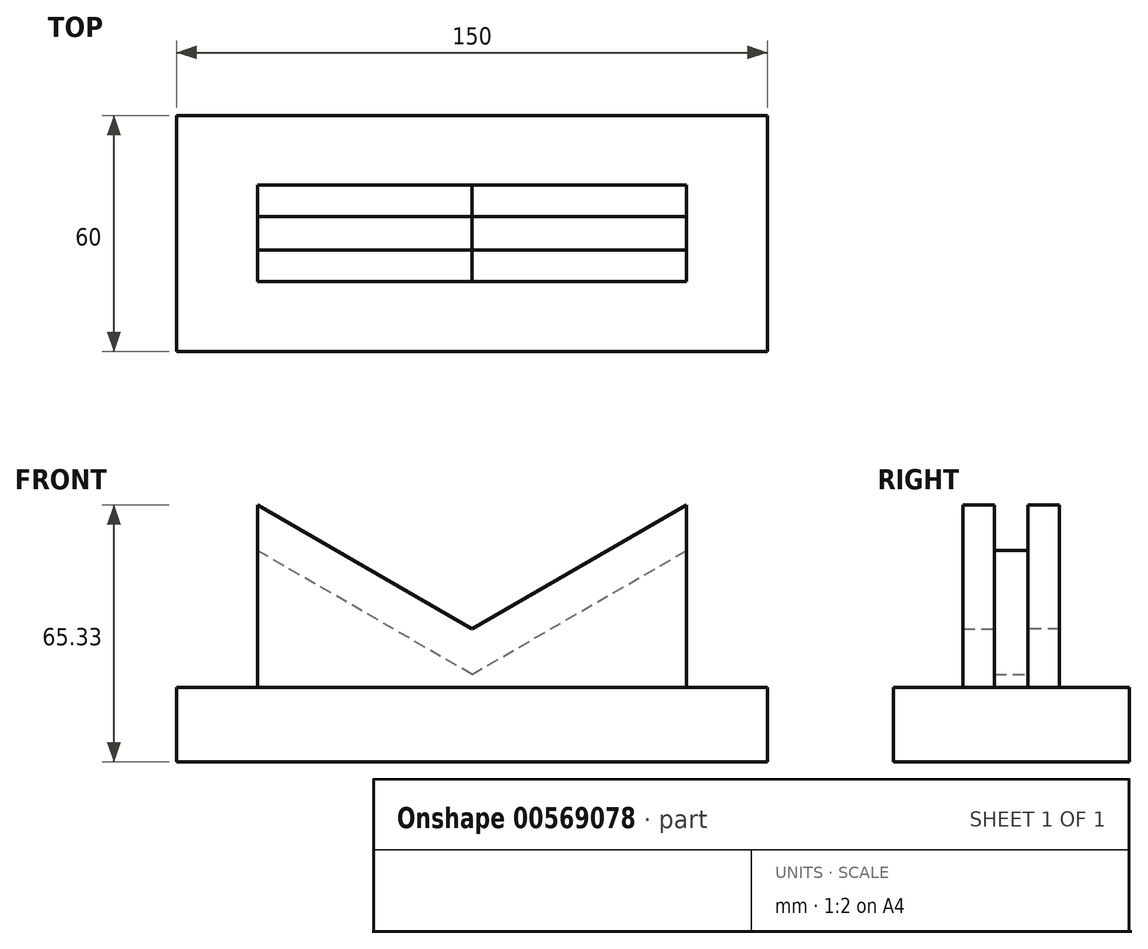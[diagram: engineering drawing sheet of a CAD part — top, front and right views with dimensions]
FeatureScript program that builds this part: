
annotation { "Feature Type Name" : "Feature", "Feature Type Description" : "" }
export const myFeature = defineFeature(function(context is Context, id is Id, definition is map)
    precondition{}
    {
        {
            var Q0;
            Q0=qCreatedBy(makeId("Front.planeOp"),FACE);
            var sketch = newSketch(context, id + "F0", { "sketchPlane" : qUnion([Q0])});
            skLineSegment(sketch, "E0.bottom", {"start": v(-75, 0) * mm, "end": v(75, 0) * mm});
            skLineSegment(sketch, "E0.top", {"start": v(-75, 19) * mm, "end": v(75, 19) * mm});
            skLineSegment(sketch, "E0.left", {"start": v(-75, 0) * mm, "end": v(-75, 19) * mm});
            skLineSegment(sketch, "E0.right", {"start": v(75, 0) * mm, "end": v(75, 19) * mm});
            skSolve(sketch);
        }
        {
            var Q0;
            Q0 = qSketchRegion(id + "F0", true);
            extrude(context, id + "F1", {"entities" : qUnion([Q0]), "endBound" : BoundingType.SYMMETRIC, "depth" : 60 * mm, "offsetDistance" : 25 * mm});
        }
        {
            var Q0;
            Q0=qCreatedBy(makeId("Front.planeOp"),FACE);
            var sketch = newSketch(context, id + "F2", { "sketchPlane" : qUnion([Q0])});
            skLineSegment(sketch, "E1", {"start": v(0, 22.3) * mm, "end": v(-54.53, 53.78) * mm});
            skLineSegment(sketch, "E2", {"start": v(-54.53, 53.78) * mm, "end": v(-54.53, 19) * mm});
            skLineSegment(sketch, "E3", {"start": v(0, 22.3) * mm, "end": v(0, 78.1) * mm, "construction": true});
            skLineSegment(sketch, "E4.MirrorCS", {"start": v(0, 22.3) * mm, "end": v(54.53, 53.78) * mm});
            skLineSegment(sketch, "E5.MirrorCS", {"start": v(54.53, 53.78) * mm, "end": v(54.53, 19) * mm});
            skPoint(sketch, "E6.orphan", {"position": v(54.53, 22.3) * mm});
            skPoint(sketch, "E7.orphan", {"position": v(-54.53, 22.3) * mm});
            skPoint(sketch, "E8.orphan", {"position": v(75, 19) * mm});
            skPoint(sketch, "E9.orphan", {"position": v(-75, 19) * mm});
            skLineSegment(sketch, "E10.0", {"start": v(-54.53, 19) * mm, "end": v(54.53, 19) * mm});
            skSolve(sketch);
        }
        {
            var Q0;
            Q0 = qSketchRegion(id + "F2", true);
            extrude(context, id + "F3", {"entities" : qUnion([Q0]), "endBound" : BoundingType.SYMMETRIC, "depth" : 8.5 * mm, "offsetDistance" : 25 * mm});
        }
        {
            var Q0;
            Q0=makeQuery(id+"F3.opExtrude","CAP_FACE",FACE,{"disambiguationData":[OSD([sQuery(id+"F2.wireOp",EDGE,"E1"),sQuery(id+"F2.wireOp",EDGE,"E2"),sQuery(id+"F2.wireOp",EDGE,"lnKhhqay-CDqk-tFTO-5ORt-z1OlfFbkKawb")])],"isStart":false});
            var sketch = newSketch(context, id + "F4", { "sketchPlane" : qUnion([Q0])});
            skLineSegment(sketch, "E11.0", {"start": v(0, 33.84) * mm, "end": v(-54.53, 65.33) * mm});
            skLineSegment(sketch, "E11.1", {"start": v(0, 33.84) * mm, "end": v(54.53, 65.33) * mm});
            skLineSegment(sketch, "E12.0", {"start": v(-54.53, 65.33) * mm, "end": v(-54.53, 19) * mm});
            skLineSegment(sketch, "E12.1", {"start": v(54.53, 65.33) * mm, "end": v(54.53, 19) * mm});
            skPoint(sketch, "E13.orphan", {"position": v(-54.53, 53.78) * mm});
            skPoint(sketch, "E14.orphan", {"position": v(54.53, 53.78) * mm});
            skLineSegment(sketch, "E15.0", {"start": v(-54.53, 19) * mm, "end": v(54.53, 19) * mm});
            skPoint(sketch, "E16.orphan", {"position": v(75, 19) * mm});
            skPoint(sketch, "E17.orphan", {"position": v(-75, 19) * mm});
            skSolve(sketch);
        }
        {
            var Q0;
            Q0 = qSketchRegion(id + "F4", true);
            extrude(context, id + "F5", {"entities" : qUnion([Q0]), "depth" : 8 * mm, "offsetDistance" : 25 * mm});
        }
        {
            var Q0;
            Q0=makeQuery(id+"F3.opExtrude","CAP_FACE",FACE,{"disambiguationData":[OSD([sQuery(id+"F2.wireOp",EDGE,"E4.MirrorCS"),sQuery(id+"F2.wireOp",EDGE,"E5.MirrorCS"),sQuery(id+"F2.wireOp",EDGE,"0fbee516-dda7-44bb-97da-947db9ab2e902.MirrorCS")])],"isStart":true});
            var sketch = newSketch(context, id + "F6", { "sketchPlane" : qUnion([Q0])});
            skLineSegment(sketch, "E18.0", {"start": v(54.53, 65.33) * mm, "end": v(54.53, 19) * mm});
            skLineSegment(sketch, "E18.1", {"start": v(0, 33.84) * mm, "end": v(54.53, 65.33) * mm});
            skLineSegment(sketch, "E18.2", {"start": v(0, 33.84) * mm, "end": v(-54.53, 65.33) * mm});
            skLineSegment(sketch, "E18.3", {"start": v(-54.53, 65.33) * mm, "end": v(-54.53, 19) * mm});
            skLineSegment(sketch, "E18.4", {"start": v(54.53, 19) * mm, "end": v(-54.53, 19) * mm});
            skSolve(sketch);
        }
        {
            var Q0;
            Q0 = qSketchRegion(id + "F6", true);
            extrude(context, id + "F7", {"entities" : qUnion([Q0]), "depth" : 8 * mm, "offsetDistance" : 25 * mm});
        }
    });
